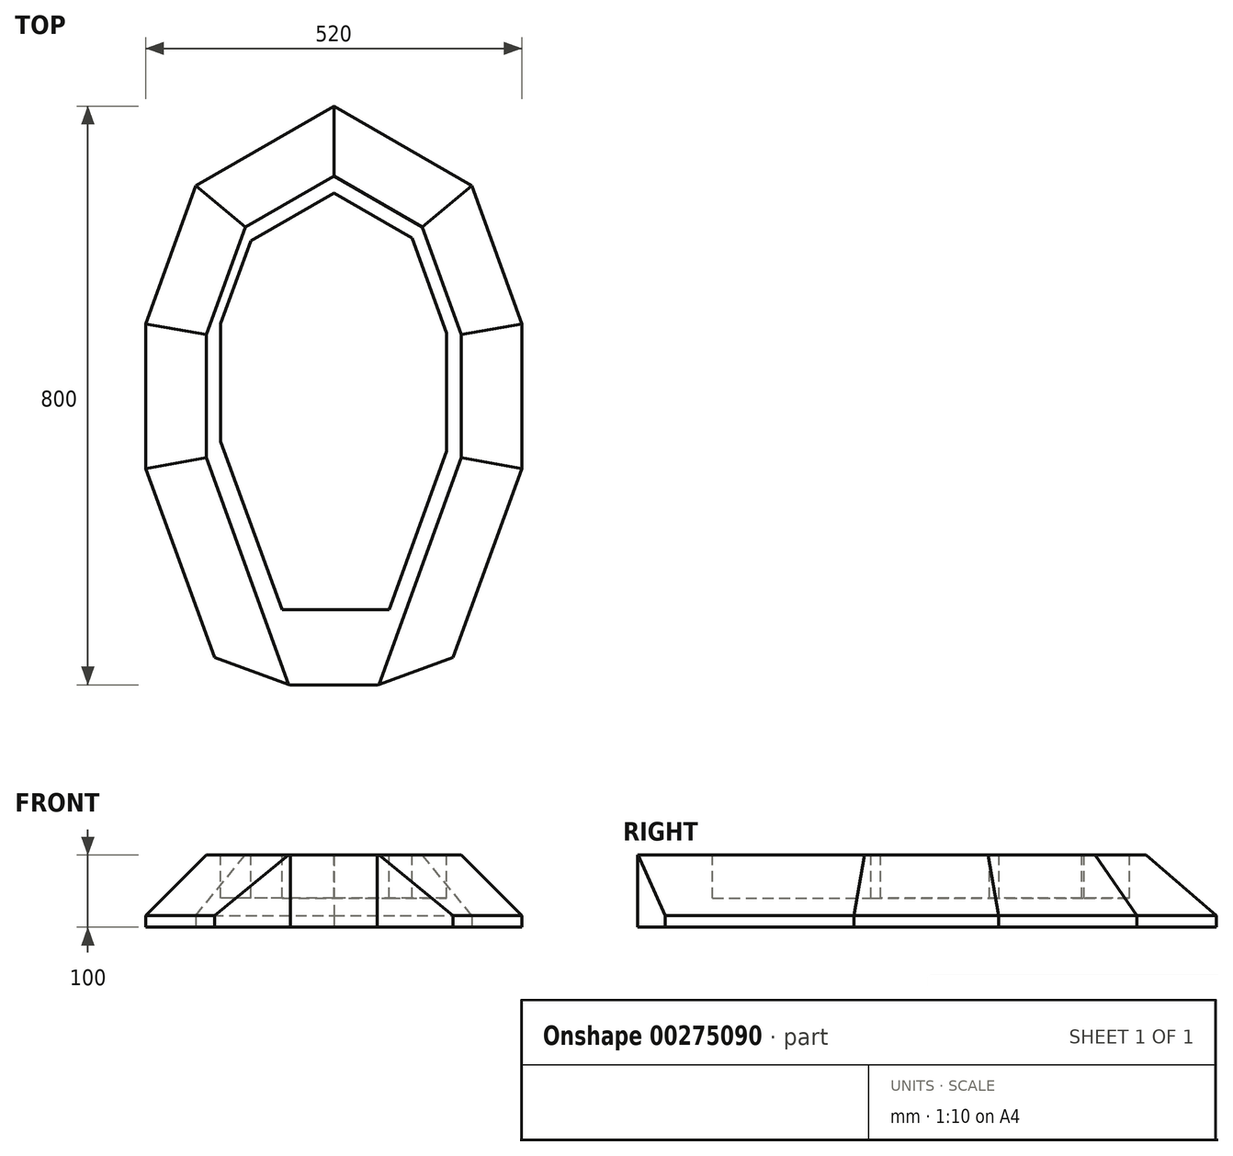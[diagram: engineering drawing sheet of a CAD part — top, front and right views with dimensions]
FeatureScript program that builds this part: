
annotation { "Feature Type Name" : "Feature", "Feature Type Description" : "" }
export const myFeature = defineFeature(function(context is Context, id is Id, definition is map)
    precondition{}
    {
        {
            var Q0;
            Q0=qCreatedBy(makeId("Top.planeOp"),FACE);
            var sketch = newSketch(context, id + "F0", { "sketchPlane" : qUnion([Q0])});
            skPoint(sketch, "E0", {"position": v(0, -400) * mm});
            skPoint(sketch, "E1", {"position": v(0, 400) * mm});
            skLineSegment(sketch, "E2", {"start": v(0, 400) * mm, "end": v(190.53, 290) * mm});
            skLineSegment(sketch, "E3", {"start": v(190.53, 290) * mm, "end": v(260, 99.12) * mm});
            skLineSegment(sketch, "E4", {"start": v(260, 99.12) * mm, "end": v(260, -100.88) * mm});
            skLineSegment(sketch, "E5", {"start": v(260, -100.88) * mm, "end": v(165.04, -361.77) * mm});
            skLineSegment(sketch, "E6.MirrorCS", {"start": v(-190.53, 290) * mm, "end": v(-260, 99.12) * mm});
            skLineSegment(sketch, "E7.MirrorCS", {"start": v(-260, 99.12) * mm, "end": v(-260, -100.88) * mm});
            skLineSegment(sketch, "E8.MirrorCS", {"start": v(-260, -100.88) * mm, "end": v(-165.04, -361.77) * mm});
            skLineSegment(sketch, "E9", {"start": v(0, 400) * mm, "end": v(-190.53, 290) * mm});
            skLineSegment(sketch, "E10", {"start": v(0, 400) * mm, "end": v(0, 0) * mm, "construction": true});
            skLineSegment(sketch, "E11", {"start": v(0, 0) * mm, "end": v(0, -400) * mm, "construction": true});
            skLineSegment(sketch, "E12", {"start": v(-60, -400) * mm, "end": v(-165.04, -361.77) * mm});
            skLineSegment(sketch, "E13", {"start": v(60, -400) * mm, "end": v(165.04, -361.77) * mm});
            skLineSegment(sketch, "E14", {"start": v(60, -400) * mm, "end": v(-60, -400) * mm});
            skSolve(sketch);
        }
        {
            var Q0;
            Q0=makeQuery(id+"F0.imprint","IMPRINT",FACE,{"disambiguationData":[TD([[makeQuery(id+"F0.imprint","IMPRINT",EDGE,{"derivedFrom":sQuery(id+"F0.wireOp",EDGE,"E2")}),-1.0]])]});
            extrude(context, id + "F1", {"entities" : qUnion([Q0]), "depth" : 10 * mm});
        }
        {
            var Q0;
            Q0=makeQuery(id+"F1.opExtrude","CAP_FACE",FACE,{"disambiguationData":[OSD([sQuery(id+"F0.wireOp",EDGE,"E2"),sQuery(id+"F0.wireOp",EDGE,"E3"),sQuery(id+"F0.wireOp",EDGE,"E4"),sQuery(id+"F0.wireOp",EDGE,"E5"),sQuery(id+"F0.wireOp",EDGE,"qnnv57Yo-jdDq-iQc0-U2FB-CUaHrvrgSZ3B"),sQuery(id+"F0.wireOp",EDGE,"E6.MirrorCS"),sQuery(id+"F0.wireOp",EDGE,"E7.MirrorCS"),sQuery(id+"F0.wireOp",EDGE,"E8.MirrorCS"),sQuery(id+"F0.wireOp",EDGE,"aVjazQxE-Lilv-1S9G-H6xv-cRvRcR3v1Ot3"),sQuery(id+"F0.wireOp",EDGE,"E9")])],"isStart":false});
            extrude(context, id + "F2", {"entities" : qUnion([Q0]), "operationType" : NewBodyOperationType.ADD, "depth" : 90 * mm});
        }
        {
            var Q0;
            Q0=makeQuery(id+"F2.opExtrude","CAP_EDGE",EDGE,{"disambiguationData":[OSD([sQuery(id+"F0.wireOp",EDGE,"aVjazQxE-Lilv-1S9G-H6xv-cRvRcR3v1Ot3")])],"isStart":false});
            var Q1;
            Q1=makeQuery(id+"F2.opExtrude","CAP_EDGE",EDGE,{"disambiguationData":[OSD([sQuery(id+"F0.wireOp",EDGE,"E8.MirrorCS")])],"isStart":false});
            var Q2;
            Q2=makeQuery(id+"F2.opExtrude","CAP_EDGE",EDGE,{"disambiguationData":[OSD([sQuery(id+"F0.wireOp",EDGE,"qnnv57Yo-jdDq-iQc0-U2FB-CUaHrvrgSZ3B")])],"isStart":false});
            var Q3;
            Q3=makeQuery(id+"F2.opExtrude","CAP_EDGE",EDGE,{"disambiguationData":[OSD([sQuery(id+"F0.wireOp",EDGE,"E5")])],"isStart":false});
            var Q4;
            Q4=makeQuery(id+"F2.opExtrude","CAP_EDGE",EDGE,{"disambiguationData":[OSD([sQuery(id+"F0.wireOp",EDGE,"E4")])],"isStart":false});
            var Q5;
            Q5=makeQuery(id+"F2.opExtrude","CAP_EDGE",EDGE,{"disambiguationData":[OSD([sQuery(id+"F0.wireOp",EDGE,"E3")])],"isStart":false});
            var Q6;
            Q6=makeQuery(id+"F2.opExtrude","CAP_EDGE",EDGE,{"disambiguationData":[OSD([sQuery(id+"F0.wireOp",EDGE,"E2")])],"isStart":false});
            var Q7;
            Q7=makeQuery(id+"F2.opExtrude","CAP_EDGE",EDGE,{"disambiguationData":[OSD([sQuery(id+"F0.wireOp",EDGE,"E9")])],"isStart":false});
            var Q8;
            Q8=makeQuery(id+"F2.opExtrude","CAP_EDGE",EDGE,{"disambiguationData":[OSD([sQuery(id+"F0.wireOp",EDGE,"E6.MirrorCS")])],"isStart":false});
            var Q9;
            Q9=makeQuery(id+"F2.opExtrude","CAP_EDGE",EDGE,{"disambiguationData":[OSD([sQuery(id+"F0.wireOp",EDGE,"E7.MirrorCS")])],"isStart":false});
            chamfer(context, id + "F3", {"entities" : qUnion([Q0, Q1, Q2, Q3, Q4, Q5, Q6, Q7, Q8, Q9]), "chamferType" : ChamferType.OFFSET_ANGLE, "width" : 83.77 * mm, "oppositeDirection" : false, "angle" : 45 * degree, "tangentPropagation" : true});
        }
        {
            var Q0;
            Q0=makeQuery(id+"F2.opExtrude","CAP_FACE",FACE,{"disambiguationData":[OSD([sQuery(id+"F0.wireOp",EDGE,"E2"),sQuery(id+"F0.wireOp",EDGE,"E3"),sQuery(id+"F0.wireOp",EDGE,"E4"),sQuery(id+"F0.wireOp",EDGE,"E5"),sQuery(id+"F0.wireOp",EDGE,"E6.MirrorCS"),sQuery(id+"F0.wireOp",EDGE,"E7.MirrorCS"),sQuery(id+"F0.wireOp",EDGE,"E8.MirrorCS"),sQuery(id+"F0.wireOp",EDGE,"E9"),sQuery(id+"F0.wireOp",EDGE,"E12"),sQuery(id+"F0.wireOp",EDGE,"E13"),sQuery(id+"F0.wireOp",EDGE,"E14")])],"isStart":false});
            var sketch = newSketch(context, id + "F4", { "sketchPlane" : qUnion([Q0])});
            skLineSegment(sketch, "E15.1", {"start": v(-156.23, 99.58) * mm, "end": v(-156.23, -63.82) * mm});
            skLineSegment(sketch, "E15.3", {"start": v(-114.57, 214.03) * mm, "end": v(-156.23, 99.58) * mm});
            skLineSegment(sketch, "E15.4", {"start": v(0, 280.18) * mm, "end": v(-114.57, 214.03) * mm});
            skLineSegment(sketch, "E15.6", {"start": v(156.23, -77.14) * mm, "end": v(156.23, 86.27) * mm});
            skLineSegment(sketch, "E15.7", {"start": v(156.23, 86.27) * mm, "end": v(108.44, 217.57) * mm});
            skLineSegment(sketch, "E15.8", {"start": v(108.44, 217.57) * mm, "end": v(0, 280.18) * mm});
            skLineSegment(sketch, "E16", {"start": v(-71.62, -296.28) * mm, "end": v(76.47, -296.28) * mm});
            skLineSegment(sketch, "E17", {"start": v(-71.62, -296.28) * mm, "end": v(-156.23, -63.82) * mm});
            skLineSegment(sketch, "E18", {"start": v(76.47, -296.28) * mm, "end": v(156.23, -77.14) * mm});
            skSolve(sketch);
        }
        {
            var Q0;
            Q0=makeQuery(id+"F4.imprint","IMPRINT",FACE,{"disambiguationData":[TD([[makeQuery(id+"F4.imprint","IMPRINT",EDGE,{"derivedFrom":sQuery(id+"F4.wireOp",EDGE,"E15.1")}),1.0]])]});
            extrude(context, id + "F5", {"entities" : qUnion([Q0]), "operationType" : NewBodyOperationType.REMOVE, "oppositeDirection" : true, "depth" : 60 * mm});
        }
    });
